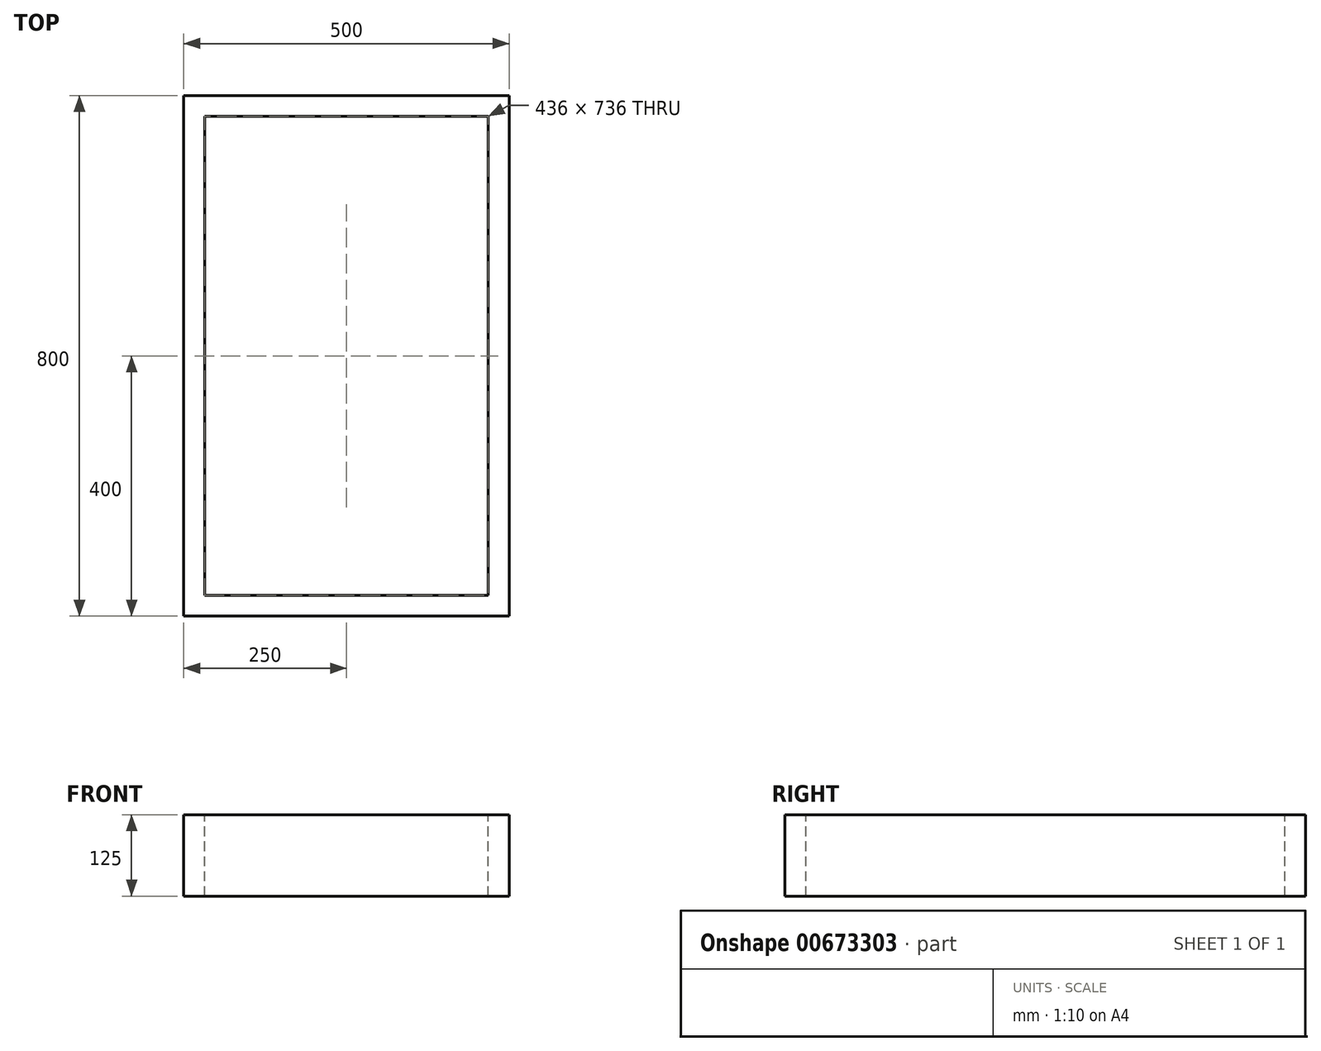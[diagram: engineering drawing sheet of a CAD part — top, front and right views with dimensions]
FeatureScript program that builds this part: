
annotation { "Feature Type Name" : "Feature", "Feature Type Description" : "" }
export const myFeature = defineFeature(function(context is Context, id is Id, definition is map)
    precondition{}
    {
        {
            var Q0;
            Q0=qCreatedBy(makeId("Top.planeOp"),FACE);
            var sketch = newSketch(context, id + "F0", { "sketchPlane" : qUnion([Q0])});
            skLineSegment(sketch, "E0.bottom", {"start": v(0, 0) * mm, "end": v(500, 0) * mm});
            skLineSegment(sketch, "E0.top", {"start": v(0, 800) * mm, "end": v(500, 800) * mm});
            skLineSegment(sketch, "E0.left", {"start": v(0, 0) * mm, "end": v(0, 800) * mm});
            skLineSegment(sketch, "E0.right", {"start": v(500, 0) * mm, "end": v(500, 800) * mm});
            skSolve(sketch);
        }
        {
            var Q0;
            Q0=qSketchRegion(id+"F0",true);
            extrude(context, id + "F1", {"entities" : qUnion([Q0]), "depth" : 125 * mm, "offsetDistance" : 25 * mm});
        }
        {
            var Q0;
            Q0=makeQuery(id+"F1.opExtrude","CAP_FACE",FACE,{"disambiguationData":[OSD([sQuery(id+"F0.wireOp",EDGE,"E0.bottom"),sQuery(id+"F0.wireOp",EDGE,"E0.top"),sQuery(id+"F0.wireOp",EDGE,"E0.left"),sQuery(id+"F0.wireOp",EDGE,"E0.right")])],"isStart":false});
            var sketch = newSketch(context, id + "F2", { "sketchPlane" : qUnion([Q0])});
            skLineSegment(sketch, "E1.bottom", {"start": v(32, 32) * mm, "end": v(468, 32) * mm});
            skLineSegment(sketch, "E1.top", {"start": v(32, 768) * mm, "end": v(468, 768) * mm});
            skLineSegment(sketch, "E1.left", {"start": v(32, 32) * mm, "end": v(32, 768) * mm});
            skLineSegment(sketch, "E1.right", {"start": v(468, 32) * mm, "end": v(468, 768) * mm});
            skSolve(sketch);
        }
        {
            var Q0;
            Q0=qSketchRegion(id+"F2",true);
            extrude(context, id + "F3", {"entities" : qUnion([Q0]), "operationType" : NewBodyOperationType.REMOVE, "endBound" : BoundingType.THROUGH_ALL, "oppositeDirection" : true, "depth" : (750 - 32) * mm, "offsetDistance" : 25 * mm});
        }
    });
